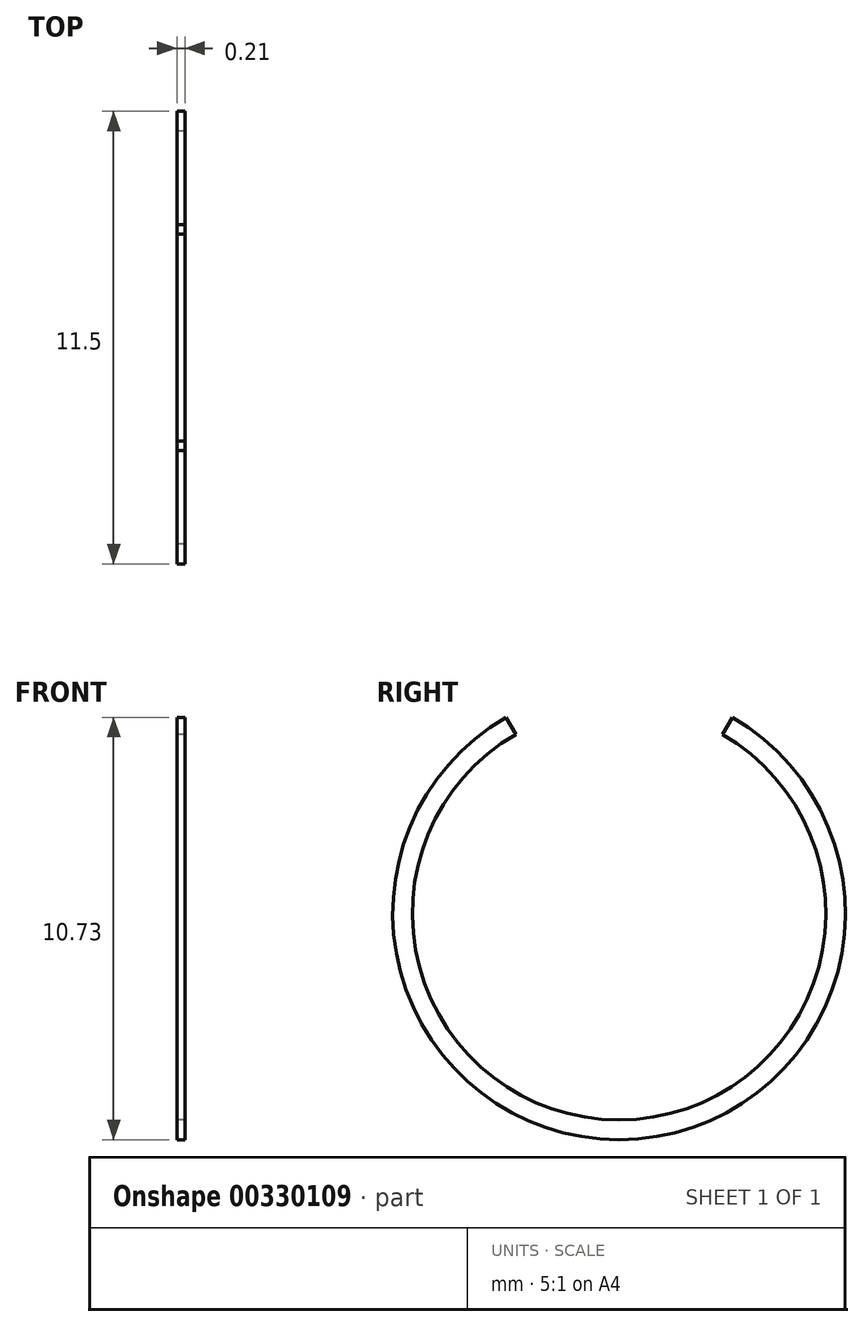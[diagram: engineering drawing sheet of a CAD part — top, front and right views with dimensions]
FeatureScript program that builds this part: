
annotation { "Feature Type Name" : "Feature", "Feature Type Description" : "" }
export const myFeature = defineFeature(function(context is Context, id is Id, definition is map)
    precondition{}
    {
        {
            var Q0;
            Q0=qCreatedBy(makeId("Front.planeOp"),FACE);
            var sketch = newSketch(context, id + "F0", { "sketchPlane" : qUnion([Q0])});
            skLineSegment(sketch, "E0", {"start": v(0, 0) * mm, "end": v(0.21, 0) * mm});
            skLineSegment(sketch, "E1", {"start": v(0.21, 0) * mm, "end": v(0.21, 0.5) * mm});
            skLineSegment(sketch, "E2", {"start": v(0.21, 0.5) * mm, "end": v(0, 0.5) * mm});
            skLineSegment(sketch, "E3", {"start": v(0, 0.5) * mm, "end": v(0, 0) * mm});
            skLineSegment(sketch, "E4", {"start": v(0, 5.75) * mm, "end": v(0.74, 5.75) * mm});
            skSolve(sketch);
        }
        {
            var Q0;
            Q0=makeQuery(id+"F0.imprint","IMPRINT",FACE,{"disambiguationData":[TD([[makeQuery(id+"F0.imprint","IMPRINT",EDGE,{"derivedFrom":sQuery(id+"F0.wireOp",EDGE,"E0")}),1.0]])]});
            var Q1;
            Q1=sQuery(id+"F0.wireOp",EDGE,"E4");
            revolve(context, id + "F1", {"entities" : qUnion([Q0]), "axis" : qUnion([Q1]), "revolveType" : RevolveType.SYMMETRIC, "angle" : 300 * degree});
        }
    });
